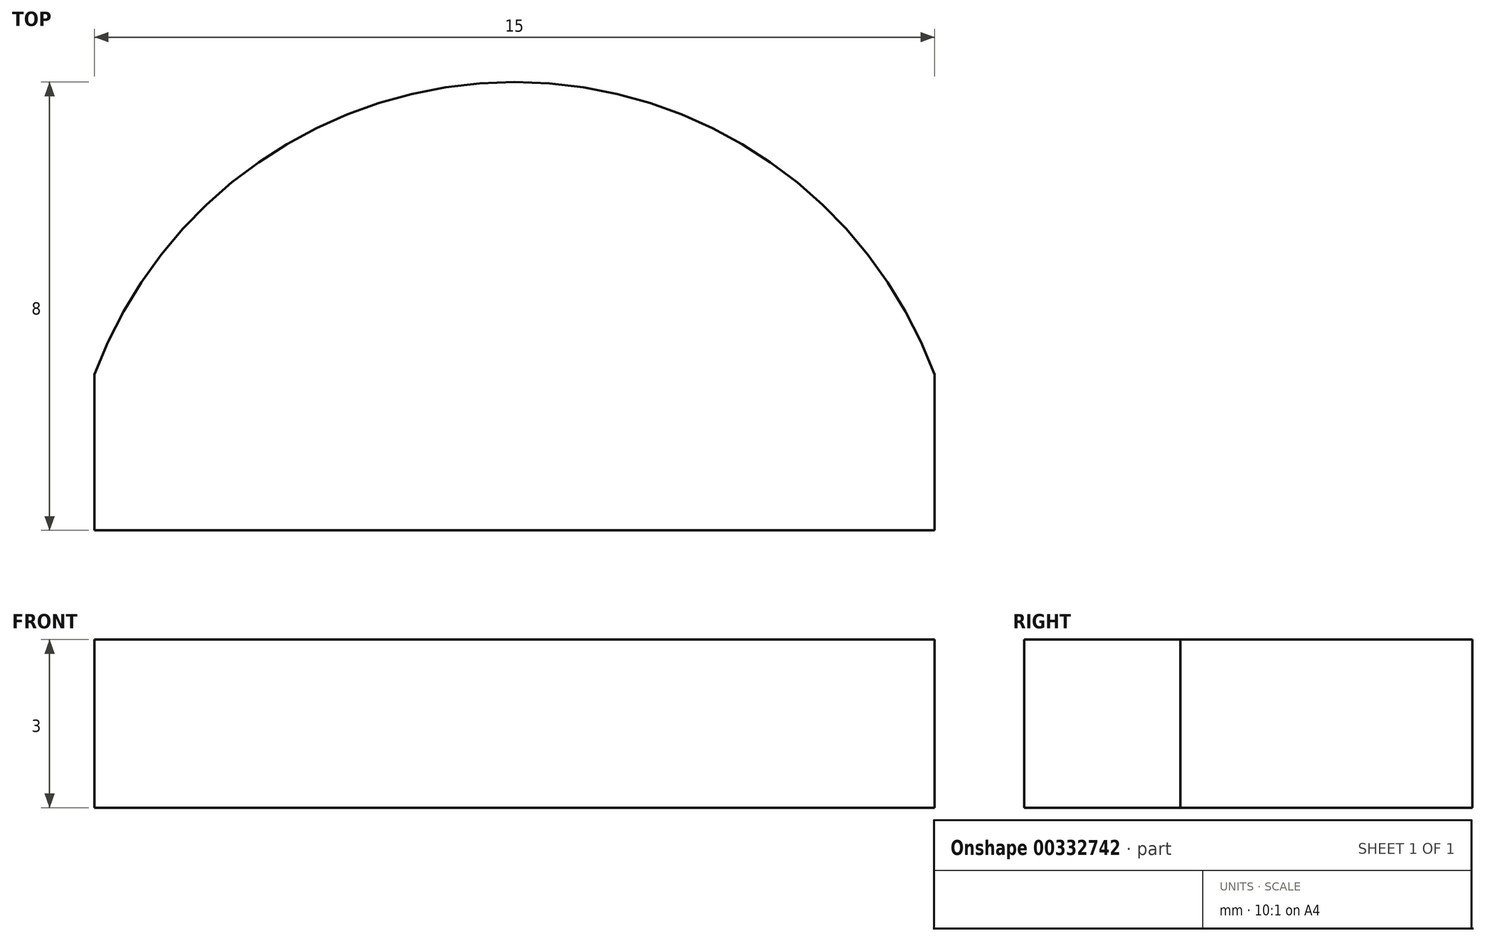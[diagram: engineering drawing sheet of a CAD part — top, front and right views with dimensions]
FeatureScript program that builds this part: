
annotation { "Feature Type Name" : "Feature", "Feature Type Description" : "" }
export const myFeature = defineFeature(function(context is Context, id is Id, definition is map)
    precondition{}
    {
        {
            var Q0;
            Q0=qCreatedBy(makeId("Top.planeOp"),FACE);
            var sketch = newSketch(context, id + "F0", { "sketchPlane" : qUnion([Q0])});
            skArc(sketch, "E0", {"start": v(7.5, 2.78) * mm, "mid": v(0, 8) * mm, "end": v(-7.5, 2.78) * mm});
            skLineSegment(sketch, "E1", {"start": v(-7.5, 0) * mm, "end": v(-7.5, 2.78) * mm});
            skLineSegment(sketch, "E2", {"start": v(7.5, 0) * mm, "end": v(7.5, 2.78) * mm});
            skLineSegment(sketch, "E3", {"start": v(-7.5, 0) * mm, "end": v(7.5, 0) * mm});
            skSolve(sketch);
        }
        {
            var Q0;
            Q0=makeQuery(id+"F0.imprint","IMPRINT",FACE,{"disambiguationData":[TD([[makeQuery(id+"F0.imprint","IMPRINT",EDGE,{"derivedFrom":sQuery(id+"F0.wireOp",EDGE,"E0")}),1.0]])]});
            extrude(context, id + "F1", {"entities" : qUnion([Q0]), "depth" : 3 * mm});
        }
    });
